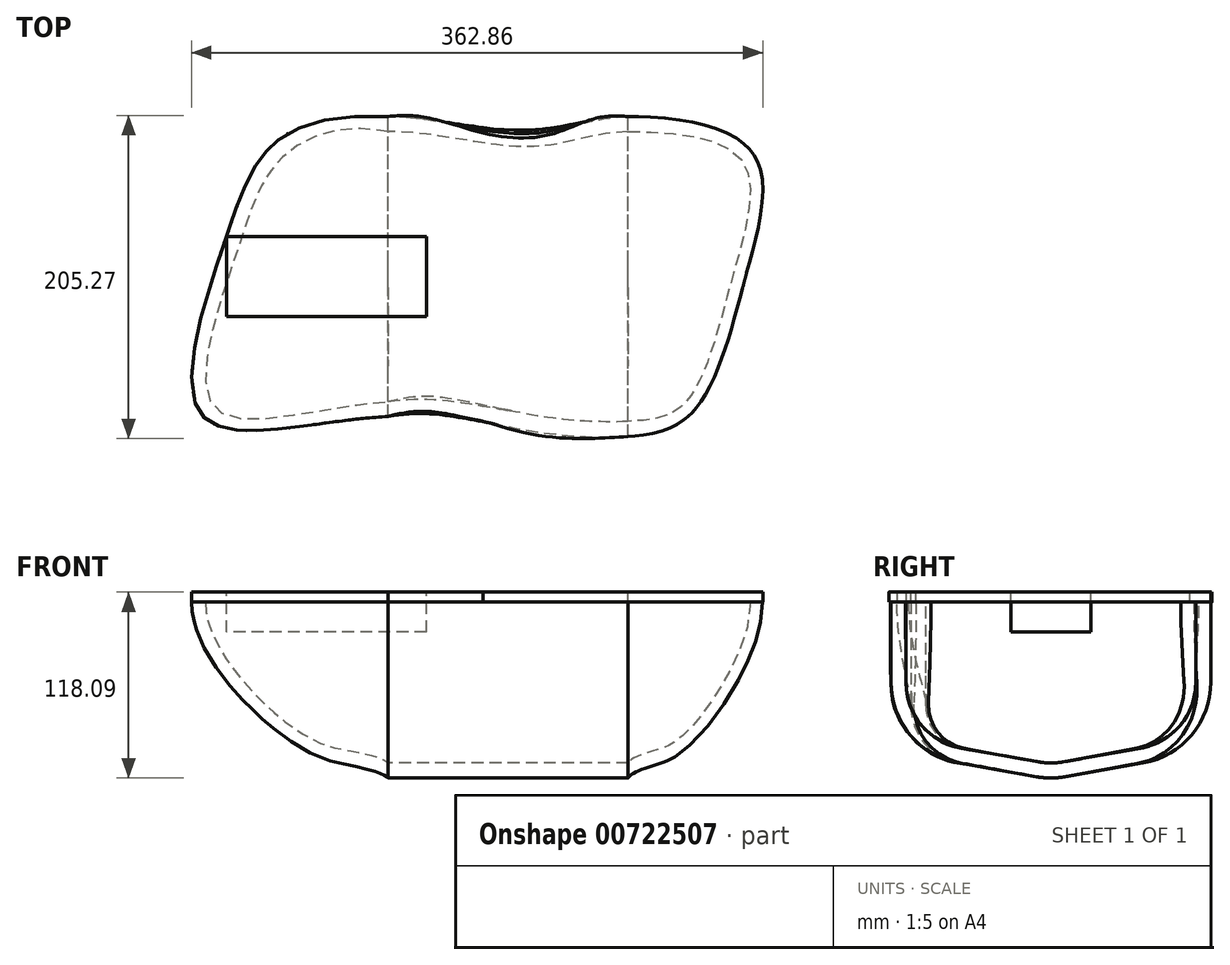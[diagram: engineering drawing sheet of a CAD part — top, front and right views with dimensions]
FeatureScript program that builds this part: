
annotation { "Feature Type Name" : "Feature", "Feature Type Description" : "" }
export const myFeature = defineFeature(function(context is Context, id is Id, definition is map)
    precondition{}
    {
        {
            var Q0;
            Q0=qCreatedBy(makeId("Right.planeOp"),FACE);
            var sketch = newSketch(context, id + "F0", { "sketchPlane" : qUnion([Q0])});
            skLineSegment(sketch, "E0", {"start": v(0, 0) * mm, "end": v(0, -9.52) * mm});
            skArc(sketch, "E1", {"start": v(0, -9.53) * mm, "mid": v(4.43, -9.33) * mm, "end": v(8.82, -8.75) * mm});
            skArc(sketch, "E2", {"start": v(0, 0) * mm, "mid": v(3.6, 0.16) * mm, "end": v(7.17, 0.63) * mm});
            skLineSegment(sketch, "E3", {"start": v(7.17, 0.63) * mm, "end": v(56.8, 9.38) * mm});
            skLineSegment(sketch, "E4", {"start": v(8.82, -8.75) * mm, "end": v(58.46, 0) * mm});
            skArc(sketch, "E5", {"start": v(58.46, 0) * mm, "mid": v(89.39, 17.85) * mm, "end": v(101.6, 51.4) * mm});
            skArc(sketch, "E6", {"start": v(56.8, 9.38) * mm, "mid": v(82.1, 23.98) * mm, "end": v(92.07, 51.4) * mm});
            skLineSegment(sketch, "E7", {"start": v(92.07, 51.4) * mm, "end": v(92.07, 102.2) * mm});
            skLineSegment(sketch, "E8", {"start": v(92.07, 102.2) * mm, "end": v(101.6, 102.2) * mm});
            skLineSegment(sketch, "E9", {"start": v(101.6, 102.2) * mm, "end": v(101.6, 51.4) * mm});
            skLineSegment(sketch, "E10", {"start": v(0, -9.52) * mm, "end": v(-91, -9.52) * mm, "construction": true});
            skSolve(sketch);
        }
        {
            var Q0;
            Q0=qCreatedBy(makeId("Right.planeOp"),FACE);
            var sketch = newSketch(context, id + "F1", { "sketchPlane" : qUnion([Q0])});
            skLineSegment(sketch, "E11", {"start": v(0, -9.52) * mm, "end": v(0, 0) * mm});
            skLineSegment(sketch, "E12", {"start": v(-7.17, 0.63) * mm, "end": v(-56.8, 9.38) * mm});
            skArc(sketch, "E13", {"start": v(-92.08, 51.4) * mm, "mid": v(-82.1, 23.98) * mm, "end": v(-56.8, 9.38) * mm});
            skLineSegment(sketch, "E14", {"start": v(-92.08, 51.4) * mm, "end": v(-92.08, 102.2) * mm});
            skLineSegment(sketch, "E15", {"start": v(-92.08, 102.2) * mm, "end": v(-101.6, 102.2) * mm});
            skLineSegment(sketch, "E16", {"start": v(-101.6, 102.2) * mm, "end": v(-101.6, 51.4) * mm});
            skArc(sketch, "E17", {"start": v(-101.6, 51.4) * mm, "mid": v(-89.39, 17.85) * mm, "end": v(-58.46, 0) * mm});
            skLineSegment(sketch, "E18", {"start": v(-58.46, 0) * mm, "end": v(-8.82, -8.75) * mm});
            skArc(sketch, "E19", {"start": v(-8.82, -8.75) * mm, "mid": v(-4.43, -9.33) * mm, "end": v(0, -9.53) * mm});
            skLineSegment(sketch, "E20", {"start": v(0, -9.52) * mm, "end": v(29.83, -9.52) * mm, "construction": true});
            skArc(sketch, "E21", {"start": v(-7.17, 0.63) * mm, "mid": v(-3.6, 0.16) * mm, "end": v(0, 0) * mm});
            skSolve(sketch);
        }
        {
            var Q0;
            Q0=sQuery(id+"F0.wireOp",EDGE,"E7");
            var Q1;
            Q1=sQuery(id+"F0.wireOp",VERTEX,"E7.end");
            cPlane(context, id + "F2", {"entities" : qUnion([Q0, Q1]), "cplaneType" : CPlaneType.LINE_POINT, "offset" : 25.4 * mm, "width" : 152.4 * mm, "height" : 152.4 * mm});
        }
        {
            var Q0;
            Q0=qCreatedBy(id+"F2.planeOp",FACE);
            var sketch = newSketch(context, id + "F3", { "sketchPlane" : qUnion([Q0])});
            skFitSpline(sketch, "E22", {"points": [v(0, 101.6) * mm, v(78.75, 78.65) * mm, v(74.62, 0) * mm, v(41, -85.92) * mm, v(0, -101.6) * mm], "startDerivative": vector(340.95, -0.61) * mm, "endDerivative": vector(-245.77, -17.3) * mm});
            skFitSpline(sketch, "E23", {"points": [v(0, 92.07) * mm, v(72.32, 73.6) * mm, v(66.35, 0) * mm, v(35.78, -80.72) * mm, v(0, -92.08) * mm], "startDerivative": vector(331.43, -3.58) * mm, "endDerivative": vector(-237.63, -13.88) * mm});
            skSolve(sketch);
        }
        {
            var Q0;
            Q0=makeQuery(id+"F0.imprint","IMPRINT",FACE,{"disambiguationData":[TD([[makeQuery(id+"F0.imprint","IMPRINT",EDGE,{"derivedFrom":sQuery(id+"F0.wireOp",EDGE,"E0")}),1.0]])]});
            var Q1;
            Q1=makeQuery(id+"F1.imprint","IMPRINT",FACE,{"disambiguationData":[TD([[makeQuery(id+"F1.imprint","IMPRINT",EDGE,{"derivedFrom":sQuery(id+"F1.wireOp",EDGE,"E11")}),1.0]])]});
            var Q2;
            Q2=sQuery(id+"F3.wireOp",EDGE,"E22");
            var Q3;
            Q3=sQuery(id+"F3.wireOp",EDGE,"E23");
            loft(context, id + "F4", {"addGuides" : true, "sheetProfilesArray" : [{ "sheetProfileEntities" : qUnion([Q0]) }, { "sheetProfileEntities" : qUnion([Q1]) }], "guidesArray" : [{ "guideEntities" : qUnion([Q2]), "guideDerivativeType" : LoftGuideDerivativeType.DEFAULT, "guideDerivativeMagnitude" : 1 }, { "guideEntities" : qUnion([Q3]), "guideDerivativeType" : LoftGuideDerivativeType.DEFAULT, "guideDerivativeMagnitude" : 1 }]});
        }
        {
            var Q0;
            Q0=qCreatedBy(makeId("Right.planeOp"),FACE);
            cPlane(context, id + "F5", {"entities" : qUnion([Q0]), "cplaneType" : CPlaneType.OFFSET, "offset" : 152.4 * mm, "oppositeDirection" : true, "width" : 152.4 * mm, "height" : 152.4 * mm});
        }
        {
            var Q0;
            Q0=qCreatedBy(id+"F5.planeOp",FACE);
            var sketch = newSketch(context, id + "F6", { "sketchPlane" : qUnion([Q0])});
            skLineSegment(sketch, "E24", {"start": v(0, 0) * mm, "end": v(0, -9.52) * mm});
            skArc(sketch, "E25", {"start": v(0, -9.52) * mm, "mid": v(4.43, -9.33) * mm, "end": v(8.82, -8.75) * mm});
            skArc(sketch, "E26", {"start": v(0, 0) * mm, "mid": v(3.6, 0.16) * mm, "end": v(7.17, 0.63) * mm});
            skLineSegment(sketch, "E27", {"start": v(7.17, 0.63) * mm, "end": v(56.8, 9.38) * mm});
            skLineSegment(sketch, "E28", {"start": v(8.82, -8.75) * mm, "end": v(58.46, 0) * mm});
            skArc(sketch, "E29", {"start": v(58.46, 0) * mm, "mid": v(89.39, 17.85) * mm, "end": v(101.6, 51.4) * mm});
            skArc(sketch, "E30", {"start": v(56.8, 9.38) * mm, "mid": v(82.1, 23.98) * mm, "end": v(92.07, 51.4) * mm});
            skLineSegment(sketch, "E31", {"start": v(92.07, 51.4) * mm, "end": v(92.07, 102.2) * mm});
            skLineSegment(sketch, "E32", {"start": v(92.07, 102.2) * mm, "end": v(101.6, 102.2) * mm});
            skLineSegment(sketch, "E33", {"start": v(101.6, 102.2) * mm, "end": v(101.6, 51.4) * mm});
            skLineSegment(sketch, "E34", {"start": v(0, -9.52) * mm, "end": v(-136.94, -9.53) * mm, "construction": true});
            skSolve(sketch);
        }
        {
            var Q0;
            Q0=qCreatedBy(id+"F5.planeOp",FACE);
            var sketch = newSketch(context, id + "F7", { "sketchPlane" : qUnion([Q0])});
            skLineSegment(sketch, "E35", {"start": v(0, -9.52) * mm, "end": v(0, 0) * mm});
            skLineSegment(sketch, "E36", {"start": v(-7.17, 0.63) * mm, "end": v(-56.8, 9.38) * mm});
            skArc(sketch, "E37", {"start": v(-79.38, 36.27) * mm, "mid": v(-72.99, 18.72) * mm, "end": v(-56.8, 9.38) * mm});
            skLineSegment(sketch, "E38", {"start": v(-79.38, 36.27) * mm, "end": v(-79.38, 102.2) * mm});
            skLineSegment(sketch, "E39", {"start": v(-79.38, 102.2) * mm, "end": v(-88.9, 102.2) * mm});
            skLineSegment(sketch, "E40", {"start": v(-88.9, 102.2) * mm, "end": v(-88.9, 36.27) * mm});
            skArc(sketch, "E41", {"start": v(-88.9, 36.27) * mm, "mid": v(-80.28, 12.6) * mm, "end": v(-58.46, 0) * mm});
            skLineSegment(sketch, "E42", {"start": v(-58.46, 0) * mm, "end": v(-8.82, -8.75) * mm});
            skArc(sketch, "E43", {"start": v(-8.82, -8.75) * mm, "mid": v(-4.43, -9.33) * mm, "end": v(0, -9.53) * mm});
            skLineSegment(sketch, "E44", {"start": v(0, -9.52) * mm, "end": v(77.95, -9.52) * mm, "construction": true});
            skArc(sketch, "E45", {"start": v(-7.17, 0.63) * mm, "mid": v(-3.6, 0.16) * mm, "end": v(0, 0) * mm});
            skSolve(sketch);
        }
        {
            var Q0;
            Q0=qCreatedBy(id+"F2.planeOp",FACE);
            var sketch = newSketch(context, id + "F8", { "sketchPlane" : qUnion([Q0])});
            skFitSpline(sketch, "E46", {"points": [v(0, 92.07) * mm, v(-45.76, 84.1) * mm, v(-84.41, 83.72) * mm, v(-152.4, 92.07) * mm], "startDerivative": vector(-181.09, -7.93) * mm, "endDerivative": vector(-183.79, -0.14) * mm});
            skFitSpline(sketch, "E47", {"points": [v(0, 101.6) * mm, v(-48.55, 92.56) * mm, v(-84.41, 91.89) * mm, v(-152.4, 101.6) * mm], "startDerivative": vector(-185.23, -9.84) * mm, "endDerivative": vector(-174.93, 2.3) * mm});
            skFitSpline(sketch, "E48", {"points": [v(0, -92.08) * mm, v(-63.05, -87.58) * mm, v(-118.7, -76.86) * mm, v(-152.4, -79.38) * mm], "startDerivative": vector(-179.44, -7.52) * mm, "endDerivative": vector(-158.43, -33.54) * mm});
            skFitSpline(sketch, "E49", {"points": [v(-152.4, -88.9) * mm, v(-119.72, -86.56) * mm, v(-66.12, -97.28) * mm, v(0, -101.6) * mm], "startDerivative": vector(156.68, 39.6) * mm, "endDerivative": vector(177.94, 10.16) * mm});
            skSolve(sketch);
        }
        {
            var Q0;
            Q0=makeQuery(id+"F0.imprint","IMPRINT",FACE,{"disambiguationData":[TD([[makeQuery(id+"F0.imprint","IMPRINT",EDGE,{"derivedFrom":sQuery(id+"F0.wireOp",EDGE,"E0")}),1.0]])]});
            var Q1;
            Q1=makeQuery(id+"F6.imprint","IMPRINT",FACE,{"disambiguationData":[TD([[makeQuery(id+"F6.imprint","IMPRINT",EDGE,{"derivedFrom":sQuery(id+"F6.wireOp",EDGE,"E24")}),1.0]])]});
            var Q2;
            Q2=sQuery(id+"F8.wireOp",EDGE,"E46");
            var Q3;
            Q3=sQuery(id+"F8.wireOp",EDGE,"E47");
            loft(context, id + "F9", {"addGuides" : true, "sheetProfilesArray" : [{ "sheetProfileEntities" : qUnion([Q0]) }, { "sheetProfileEntities" : qUnion([Q1]) }], "guidesArray" : [{ "guideEntities" : qUnion([Q2]), "guideDerivativeType" : LoftGuideDerivativeType.DEFAULT, "guideDerivativeMagnitude" : 1 }, { "guideEntities" : qUnion([Q3]), "guideDerivativeType" : LoftGuideDerivativeType.DEFAULT, "guideDerivativeMagnitude" : 1 }]});
        }
        {
            var Q1;
            Q1=makeQuery(id+"F1.imprint","IMPRINT",FACE,{"disambiguationData":[TD([[makeQuery(id+"F1.imprint","IMPRINT",EDGE,{"derivedFrom":sQuery(id+"F1.wireOp",EDGE,"E11")}),1.0]])]});
            var Q2;
            Q2=makeQuery(id+"F7.imprint","IMPRINT",FACE,{"disambiguationData":[TD([[makeQuery(id+"F7.imprint","IMPRINT",EDGE,{"derivedFrom":sQuery(id+"F7.wireOp",EDGE,"E35")}),1.0]])]});
            var Q3;
            Q3=sQuery(id+"F8.wireOp",EDGE,"E48");
            var Q4;
            Q4=sQuery(id+"F8.wireOp",EDGE,"E49");
            loft(context, id + "F10", {"operationType" : NewBodyOperationType.ADD, "addGuides" : true, "sheetProfilesArray" : [{ "sheetProfileEntities" : qUnion([Q1]) }, { "sheetProfileEntities" : qUnion([Q2]) }], "guidesArray" : [{ "guideEntities" : qUnion([Q3]), "guideDerivativeType" : LoftGuideDerivativeType.DEFAULT, "guideDerivativeMagnitude" : 1 }, { "guideEntities" : qUnion([Q4]), "guideDerivativeType" : LoftGuideDerivativeType.DEFAULT, "guideDerivativeMagnitude" : 1 }]});
        }
        {
            var Q0;
            Q0=qCreatedBy(id+"F2.planeOp",FACE);
            var sketch = newSketch(context, id + "F11", { "sketchPlane" : qUnion([Q0])});
            skFitSpline(sketch, "E50", {"points": [v(-152.4, 92.07) * mm, v(-221.69, 73.61) * mm, v(-248.57, 15.71) * mm, v(-262.8, -83.14) * mm, v(-152.4, -79.38) * mm], "startDerivative": vector(-428.17, 83.43) * mm, "endDerivative": vector(446.46, 27.33) * mm});
            skFitSpline(sketch, "E51", {"points": [v(-152.4, -88.9) * mm, v(-270.92, -87.92) * mm, v(-256.38, 21.68) * mm, v(-231.92, 77.02) * mm, v(-152.4, 101.6) * mm], "startDerivative": vector(-502.73, -25.6) * mm, "endDerivative": vector(618.11, -18.35) * mm});
            skSolve(sketch);
        }
        {
            var Q1;
            Q1 = qSketchRegion(id + "F6", true);
            var Q2;
            Q2 = qSketchRegion(id + "F7", true);
            var Q3;
            Q3=sQuery(id+"F11.wireOp",EDGE,"E51");
            var Q4;
            Q4=sQuery(id+"F11.wireOp",EDGE,"E50");
            loft(context, id + "F12", {"operationType" : NewBodyOperationType.ADD, "addGuides" : true, "sheetProfilesArray" : [{ "sheetProfileEntities" : qUnion([Q1]) }, { "sheetProfileEntities" : qUnion([Q2]) }], "guidesArray" : [{ "guideEntities" : qUnion([Q3]), "guideDerivativeType" : LoftGuideDerivativeType.DEFAULT, "guideDerivativeMagnitude" : 1 }, { "guideEntities" : qUnion([Q4]), "guideDerivativeType" : LoftGuideDerivativeType.DEFAULT, "guideDerivativeMagnitude" : 1 }]});
        }
        {
            var Q0;
            {var subQ0=sQuery(id+"F7.wireOp",EDGE,"E39");var subQ1=sQuery(id+"F6.wireOp",EDGE,"E32");var subQ2=sQuery(id+"F6.wireOp",EDGE,"E31");Q0=makeQuery(id+"F12.boolean.opBoolean","MERGE",FACE,{"derivedFrom":[makeQuery(id+"F9.opLoft","SWEPT_FACE",FACE,{"disambiguationData":[OSD([sQuery(id+"F0.wireOp",EDGE,"E7"),sQuery(id+"F0.wireOp",EDGE,"E8"),subQ2,subQ1,sQuery(id+"F8.wireOp",EDGE,"E46"),sQuery(id+"F8.wireOp",EDGE,"E47")])]}),makeQuery(id+"F10.opLoft","SWEPT_FACE",FACE,{"disambiguationData":[OSD([sQuery(id+"F1.wireOp",EDGE,"E15"),subQ0,sQuery(id+"F8.wireOp",EDGE,"E48"),sQuery(id+"F8.wireOp",EDGE,"E49")])]}),makeQuery(id+"F12.opLoft","SWEPT_FACE",FACE,{"disambiguationData":[OSD([subQ2,subQ1,subQ0,sQuery(id+"F11.wireOp",EDGE,"E50"),sQuery(id+"F11.wireOp",EDGE,"E51")])]})]});}
            var sketch = newSketch(context, id + "F13", { "sketchPlane" : qUnion([Q0])});
            skFitSpline(sketch, "E52.0", {"points": [v(-152.4, 101.6) * mm, v(-158.74, 101.79) * mm, v(-164.67, 101.77) * mm, v(-170.2, 101.56) * mm, v(-175.54, 101.34) * mm, v(-180.53, 100.94) * mm, v(-185.15, 100.35) * mm, v(-189.61, 99.77) * mm, v(-193.77, 99.02) * mm, v(-197.6, 98.08) * mm, v(-201.3, 97.19) * mm, v(-204.72, 96.12) * mm, v(-207.88, 94.87) * mm, v(-210.9, 93.7) * mm, v(-213.7, 92.34) * mm, v(-216.3, 90.82) * mm, v(-218.74, 89.4) * mm, v(-221.04, 87.8) * mm, v(-223.18, 86.05) * mm, v(-224.2, 85.21) * mm, v(-225.19, 84.34) * mm, v(-226.15, 83.42) * mm, v(-227.07, 82.54) * mm, v(-227.97, 81.61) * mm, v(-228.86, 80.65) * mm, v(-229.7, 79.73) * mm, v(-230.52, 78.76) * mm, v(-231.34, 77.75) * mm, v(-232.13, 76.77) * mm, v(-232.9, 75.77) * mm, v(-233.65, 74.73) * mm, v(-235.1, 72.72) * mm, v(-236.5, 70.58) * mm, v(-237.82, 68.3) * mm, v(-239.09, 66.12) * mm, v(-240.34, 63.75) * mm, v(-241.56, 61.21) * mm, v(-242.7, 58.82) * mm, v(-243.87, 56.18) * mm, v(-245.05, 53.3) * mm, v(-246.13, 50.68) * mm, v(-247.27, 47.72) * mm, v(-248.48, 44.43) * mm, v(-249.03, 42.93) * mm, v(-249.61, 41.31) * mm, v(-250.23, 39.58) * mm, v(-250.78, 38.02) * mm, v(-251.38, 36.3) * mm, v(-252.03, 34.42) * mm, v(-252.58, 32.84) * mm, v(-253.2, 31.02) * mm, v(-253.9, 28.95) * mm, v(-254.35, 27.67) * mm, v(-255, 25.73) * mm, v(-255.89, 23.13) * mm, v(-257.1, 19.54) * mm, v(-257.8, 17.48) * mm, v(-257.98, 16.96) * mm, v(-258.81, 14.52) * mm, v(-259.54, 12.35) * mm, v(-260.17, 10.47) * mm, v(-260.97, 8.08) * mm, v(-261.71, 5.83) * mm, v(-262.4, 3.72) * mm, v(-263.2, 1.3) * mm, v(-263.94, -1.02) * mm, v(-264.64, -3.23) * mm, v(-266.24, -8.31) * mm, v(-267.67, -13.07) * mm, v(-268.92, -17.5) * mm, v(-270.37, -22.59) * mm, v(-271.61, -27.38) * mm, v(-272.67, -31.86) * mm, v(-273.84, -36.84) * mm, v(-274.78, -41.5) * mm, v(-275.5, -45.85) * mm, v(-276.28, -50.58) * mm, v(-276.8, -54.96) * mm, v(-277.05, -58.99) * mm, v(-277.33, -63.32) * mm, v(-277.3, -67.25) * mm, v(-276.96, -70.8) * mm, v(-276.6, -74.57) * mm, v(-275.9, -77.9) * mm, v(-274.86, -80.8) * mm, v(-274.31, -82.32) * mm, v(-273.67, -83.72) * mm, v(-272.94, -85) * mm, v(-272.19, -86.3) * mm, v(-271.33, -87.48) * mm, v(-270.38, -88.55) * mm, v(-269.43, -89.6) * mm, v(-268.35, -90.57) * mm, v(-267.16, -91.45) * mm, v(-266, -92.3) * mm, v(-264.71, -93.06) * mm, v(-263.31, -93.73) * mm, v(-261.95, -94.39) * mm, v(-260.48, -94.96) * mm, v(-258.88, -95.46) * mm, v(-257.34, -95.93) * mm, v(-255.69, -96.34) * mm, v(-253.92, -96.67) * mm, v(-252.21, -96.99) * mm, v(-250.4, -97.24) * mm, v(-248.46, -97.42) * mm, v(-246.6, -97.6) * mm, v(-244.63, -97.72) * mm, v(-242.55, -97.77) * mm, v(-240.56, -97.82) * mm, v(-238.46, -97.82) * mm, v(-236.23, -97.76) * mm, v(-234.13, -97.7) * mm, v(-231.9, -97.6) * mm, v(-229.55, -97.45) * mm, v(-227.36, -97.3) * mm, v(-225.03, -97.11) * mm, v(-222.55, -96.88) * mm, v(-220.3, -96.66) * mm, v(-217.87, -96.4) * mm, v(-215.28, -96.1) * mm, v(-213, -95.85) * mm, v(-210.5, -95.54) * mm, v(-207.77, -95.2) * mm, v(-205.62, -94.91) * mm, v(-203.06, -94.58) * mm, v(-200.08, -94.17) * mm, v(-199.1, -94.04) * mm, v(-197.8, -93.87) * mm, v(-196.17, -93.65) * mm, v(-194.17, -93.37) * mm, v(-192.86, -93.2) * mm, v(-192.24, -93.11) * mm, v(-189.11, -92.69) * mm, v(-186.47, -92.34) * mm, v(-184.3, -92.05) * mm, v(-181.4, -91.68) * mm, v(-178.73, -91.34) * mm, v(-176.3, -91.05) * mm, v(-173.47, -90.71) * mm, v(-170.8, -90.42) * mm, v(-168.29, -90.16) * mm, v(-165.5, -89.87) * mm, v(-162.84, -89.63) * mm, v(-160.3, -89.42) * mm, v(-157.56, -89.2) * mm, v(-154.93, -89.03) * mm, v(-152.4, -88.9) * mm]});
            skFitSpline(sketch, "E52.1.4", {"points": [v(0, -101.6) * mm, v(-7.41, -102.02) * mm, v(-22.03, -102.22) * mm, v(-39.93, -101) * mm, v(-54.14, -99.25) * mm, v(-64.77, -97.57) * mm, v(-75.4, -95.56) * mm, v(-85.88, -93.36) * mm, v(-95.99, -91.15) * mm, v(-103.95, -89.44) * mm, v(-109.95, -88.23) * mm, v(-114.23, -87.43) * mm, v(-118.28, -86.76) * mm, v(-122.07, -86.23) * mm, v(-125.63, -85.86) * mm, v(-129.07, -85.67) * mm, v(-132.49, -85.66) * mm, v(-137.12, -85.92) * mm, v(-143.3, -86.77) * mm, v(-149.14, -88.07) * mm, v(-152.4, -88.9) * mm]});
            skFitSpline(sketch, "E52.2", {"points": [v(-152.4, -88.9) * mm, v(-138.34, -85.35) * mm, v(-120.82, -84.55) * mm, v(-64.12, -99.52) * mm, v(-22.71, -102.9) * mm, v(0, -101.6) * mm]});
            skFitSpline(sketch, "E52.4", {"points": [v(0, 101.6) * mm, v(-20.37, 100.52) * mm, v(-47.71, 90.67) * mm, v(-84.94, 89.57) * mm, v(-129.72, 101.3) * mm, v(-152.4, 101.6) * mm]});
            skFitSpline(sketch, "E53.0", {"points": [v(0, 101.6) * mm, v(7.1, 101.59) * mm, v(18.2, 101.16) * mm, v(32.81, 99.44) * mm, v(43.4, 97.51) * mm, v(53.34, 94.86) * mm, v(62.37, 91.4) * mm, v(68.9, 87.78) * mm, v(73.4, 84.41) * mm, v(76.37, 81.63) * mm, v(78.9, 78.6) * mm, v(80.98, 75.29) * mm, v(82.61, 71.73) * mm, v(84.25, 66.66) * mm, v(85.34, 59.76) * mm, v(85.36, 50.7) * mm, v(84.31, 40.98) * mm, v(82.42, 30.7) * mm, v(79.92, 19.99) * mm, v(77.52, 10.8) * mm, v(75.51, 3.34) * mm, v(73.5, -4.17) * mm, v(70.99, -13.6) * mm, v(67.92, -24.83) * mm, v(64.75, -35.81) * mm, v(61.4, -46.38) * mm, v(57.83, -56.37) * mm, v(53.96, -65.62) * mm, v(49.74, -73.97) * mm, v(45.88, -80.03) * mm, v(42.55, -84.27) * mm, v(39.93, -87.11) * mm, v(37.18, -89.62) * mm, v(33.36, -92.56) * mm, v(28.28, -95.5) * mm, v(21.75, -98.07) * mm, v(12.54, -100.42) * mm, v(5.12, -101.24) * mm, v(0, -101.6) * mm]});
            skSolve(sketch);
        }
        {
            var Q0;
            Q0 = qSketchRegion(id + "F13", true);
            extrude(context, id + "F14", {"entities" : qUnion([Q0]), "depth" : 6.35 * mm, "offsetDistance" : 25.4 * mm});
        }
        {
            var Q0;
            Q0=makeQuery(id+"F14.opExtrude","CAP_FACE",FACE,{"disambiguationData":[OSD([sQuery(id+"F13.wireOp",EDGE,"E52.0"),sQuery(id+"F13.wireOp",EDGE,"E52.2"),sQuery(id+"F13.wireOp",EDGE,"E52.4"),sQuery(id+"F13.wireOp",EDGE,"E53.0")])],"isStart":false});
            var sketch = newSketch(context, id + "F15", { "sketchPlane" : qUnion([Q0])});
            skLineSegment(sketch, "E54", {"start": v(0, 0) * mm, "end": v(-128.12, 0) * mm, "construction": true});
            skLineSegment(sketch, "E55.bottom", {"start": v(-128.12, 25.4) * mm, "end": v(-255.12, 25.4) * mm});
            skLineSegment(sketch, "E55.top", {"start": v(-128.12, -25.4) * mm, "end": v(-255.12, -25.4) * mm});
            skLineSegment(sketch, "E55.left", {"start": v(-128.12, 25.4) * mm, "end": v(-128.12, -25.4) * mm});
            skLineSegment(sketch, "E55.right", {"start": v(-255.12, 25.4) * mm, "end": v(-255.12, -25.4) * mm});
            skSolve(sketch);
        }
        {
            var Q0;
            Q0 = qSketchRegion(id + "F15", true);
            var Q1;
            Q1=makeQuery(id+"F10.opLoft","SWEPT_FACE",FACE,{"disambiguationData":[OSD([sQuery(id+"F1.wireOp",EDGE,"E11"),sQuery(id+"F1.wireOp",EDGE,"E18"),sQuery(id+"F1.wireOp",EDGE,"E19"),sQuery(id+"F7.wireOp",EDGE,"E35"),sQuery(id+"F7.wireOp",EDGE,"E42"),sQuery(id+"F7.wireOp",EDGE,"E43")])]});
            extrude(context, id + "F16", {"entities" : qUnion([Q0]), "oppositeDirection" : true, "depth" : 25.4 * mm, "endBoundEntityFace" : qUnion([Q1]), "offsetDistance" : 25.4 * mm});
        }
    });
